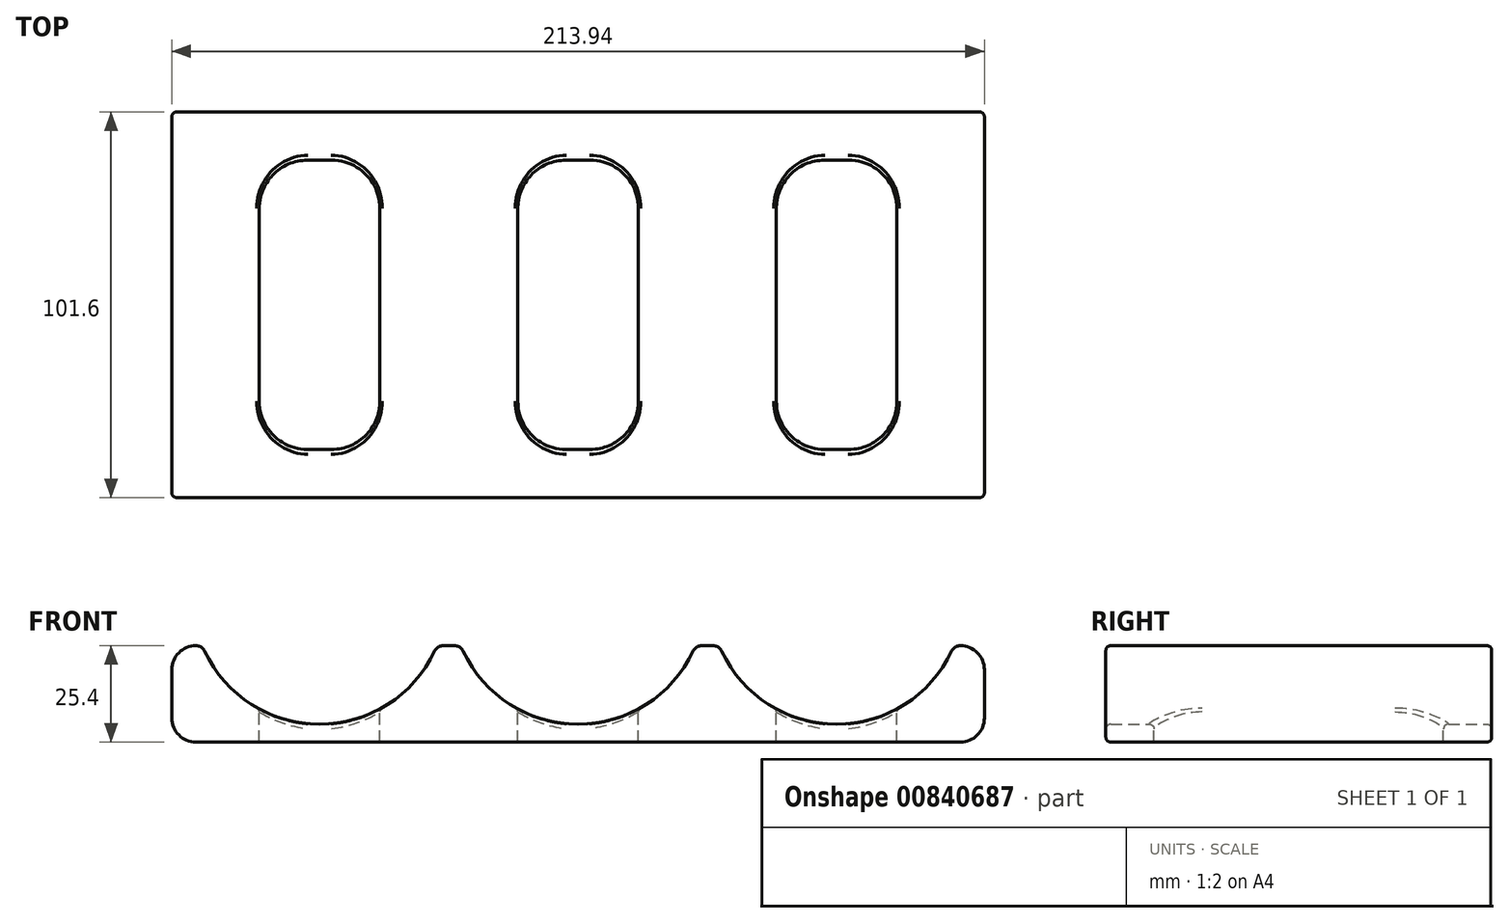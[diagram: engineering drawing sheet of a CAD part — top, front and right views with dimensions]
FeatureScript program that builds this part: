
annotation { "Feature Type Name" : "Feature", "Feature Type Description" : "" }
export const myFeature = defineFeature(function(context is Context, id is Id, definition is map)
    precondition{}
    {
        {
            var Q0;
            Q0=qCreatedBy(makeId("Front.planeOp"),FACE);
            var sketch = newSketch(context, id + "F0", { "sketchPlane" : qUnion([Q0])});
            skCircle(sketch, "E0", {"center": v(0, 0) * mm, "radius": 33.4 * mm, "construction": true});
            skCircle(sketch, "E1", {"center": v(-68.07, 0) * mm, "radius": 33.4 * mm, "construction": true});
            skCircle(sketch, "E2", {"center": v(68.07, 0) * mm, "radius": 33.4 * mm, "construction": true});
            skArc(sketch, "E3", {"start": v(-37.82, -14.16) * mm, "mid": v(-68.07, -33.4) * mm, "end": v(-98.32, -14.16) * mm});
            skArc(sketch, "E4", {"start": v(30.25, -14.16) * mm, "mid": v(0, -33.4) * mm, "end": v(-30.25, -14.16) * mm});
            skArc(sketch, "E5", {"start": v(98.32, -14.16) * mm, "mid": v(68.07, -33.4) * mm, "end": v(37.82, -14.16) * mm});
            skLineSegment(sketch, "E6", {"start": v(-100.62, -12.7) * mm, "end": v(-100.62, -12.7) * mm});
            skLineSegment(sketch, "E7", {"start": v(-100.62, -38.1) * mm, "end": v(100.62, -38.1) * mm});
            skLineSegment(sketch, "E8", {"start": v(-106.97, -19.05) * mm, "end": v(-106.97, -31.75) * mm});
            skLineSegment(sketch, "E9", {"start": v(106.97, -19.05) * mm, "end": v(106.97, -31.75) * mm});
            skPoint(sketch, "E10.orphan", {"position": v(-101.47, 0) * mm});
            skPoint(sketch, "E11.orphan", {"position": v(-34.67, 0) * mm});
            skPoint(sketch, "E12.orphan", {"position": v(-33.4, 0) * mm});
            skPoint(sketch, "E13.orphan", {"position": v(33.4, 0) * mm});
            skPoint(sketch, "E14.orphan", {"position": v(34.67, 0) * mm});
            skPoint(sketch, "E15.orphan", {"position": v(101.47, 0) * mm});
            skLineSegment(sketch, "E16.trimOffspring", {"start": v(-35.52, -12.7) * mm, "end": v(-32.55, -12.7) * mm});
            skLineSegment(sketch, "E17.trimOffspring", {"start": v(32.55, -12.7) * mm, "end": v(35.52, -12.7) * mm});
            skLineSegment(sketch, "E18.trimOffspring", {"start": v(100.62, -12.7) * mm, "end": v(100.62, -12.7) * mm});
            skPoint(sketch, "E19.visualSharp", {"position": v(-98.96, -12.7) * mm});
            skArc(sketch, "E19.filletArc", {"start": v(-98.32, -14.16) * mm, "mid": v(-99.26, -13.1) * mm, "end": v(-100.62, -12.7) * mm});
            skPoint(sketch, "E20.visualSharp", {"position": v(-37.18, -12.7) * mm});
            skArc(sketch, "E20.filletArc", {"start": v(-35.52, -12.7) * mm, "mid": v(-36.89, -13.1) * mm, "end": v(-37.82, -14.16) * mm});
            skPoint(sketch, "E21.visualSharp", {"position": v(-30.9, -12.7) * mm});
            skArc(sketch, "E21.filletArc", {"start": v(-30.25, -14.16) * mm, "mid": v(-31.19, -13.1) * mm, "end": v(-32.55, -12.7) * mm});
            skPoint(sketch, "E22.visualSharp", {"position": v(30.9, -12.7) * mm});
            skArc(sketch, "E22.filletArc", {"start": v(32.55, -12.7) * mm, "mid": v(31.19, -13.1) * mm, "end": v(30.25, -14.16) * mm});
            skPoint(sketch, "E23.visualSharp", {"position": v(37.18, -12.7) * mm});
            skArc(sketch, "E23.filletArc", {"start": v(37.82, -14.16) * mm, "mid": v(36.89, -13.1) * mm, "end": v(35.52, -12.7) * mm});
            skPoint(sketch, "E24.visualSharp", {"position": v(98.96, -12.7) * mm});
            skArc(sketch, "E24.filletArc", {"start": v(100.62, -12.7) * mm, "mid": v(99.26, -13.1) * mm, "end": v(98.32, -14.16) * mm});
            skPoint(sketch, "E25.visualSharp", {"position": v(106.97, -12.7) * mm});
            skArc(sketch, "E25.filletArc", {"start": v(106.97, -19.05) * mm, "mid": v(105.11, -14.56) * mm, "end": v(100.62, -12.7) * mm});
            skPoint(sketch, "E26.visualSharp", {"position": v(106.97, -38.1) * mm});
            skArc(sketch, "E26.filletArc", {"start": v(100.62, -38.1) * mm, "mid": v(105.11, -36.24) * mm, "end": v(106.97, -31.75) * mm});
            skPoint(sketch, "E27.visualSharp", {"position": v(-106.97, -38.1) * mm});
            skArc(sketch, "E27.filletArc", {"start": v(-106.97, -31.75) * mm, "mid": v(-105.11, -36.24) * mm, "end": v(-100.62, -38.1) * mm});
            skPoint(sketch, "E28.visualSharp", {"position": v(-106.97, -12.7) * mm});
            skArc(sketch, "E28.filletArc", {"start": v(-100.62, -12.7) * mm, "mid": v(-105.11, -14.56) * mm, "end": v(-106.97, -19.05) * mm});
            skSolve(sketch);
        }
        {
            var Q0;
            Q0 = qSketchRegion(id + "F0", true);
            extrude(context, id + "F1", {"entities" : qUnion([Q0]), "depth" : 101.6 * mm, "offsetDistance" : 25.4 * mm});
        }
        {
            var Q0;
            Q0=qCreatedBy(makeId("Top.planeOp"),FACE);
            var sketch = newSketch(context, id + "F2", { "sketchPlane" : qUnion([Q0])});
            skLineSegment(sketch, "E29.bottom", {"start": v(-15.88, -12.7) * mm, "end": v(15.88, -12.7) * mm});
            skLineSegment(sketch, "E29.top", {"start": v(-15.87, -88.9) * mm, "end": v(15.87, -88.9) * mm});
            skLineSegment(sketch, "E29.left", {"start": v(-15.88, -12.7) * mm, "end": v(-15.87, -88.9) * mm});
            skLineSegment(sketch, "E29.right", {"start": v(15.88, -12.7) * mm, "end": v(15.87, -88.9) * mm});
            skLineSegment(sketch, "E30.bottom", {"start": v(52.2, -12.7) * mm, "end": v(83.95, -12.7) * mm});
            skLineSegment(sketch, "E30.top", {"start": v(52.2, -88.9) * mm, "end": v(83.95, -88.9) * mm});
            skLineSegment(sketch, "E30.left", {"start": v(52.2, -12.7) * mm, "end": v(52.2, -88.9) * mm});
            skLineSegment(sketch, "E30.right", {"start": v(83.95, -12.7) * mm, "end": v(83.95, -88.9) * mm});
            skLineSegment(sketch, "E31.bottom", {"start": v(-83.95, -12.7) * mm, "end": v(-52.2, -12.7) * mm});
            skLineSegment(sketch, "E31.top", {"start": v(-83.95, -88.9) * mm, "end": v(-52.2, -88.9) * mm});
            skLineSegment(sketch, "E31.left", {"start": v(-83.95, -12.7) * mm, "end": v(-83.95, -88.9) * mm});
            skLineSegment(sketch, "E31.right", {"start": v(-52.2, -12.7) * mm, "end": v(-52.2, -88.9) * mm});
            skPoint(sketch, "E32", {"position": v(68.07, -12.7) * mm});
            skPoint(sketch, "E33", {"position": v(0, -12.7) * mm});
            skPoint(sketch, "E34", {"position": v(-68.07, -12.7) * mm});
            skSolve(sketch);
        }
        {
            var Q0;
            Q0 = qSketchRegion(id + "F2", true);
            extrude(context, id + "F3", {"entities" : qUnion([Q0]), "operationType" : NewBodyOperationType.REMOVE, "endBound" : BoundingType.THROUGH_ALL, "oppositeDirection" : true, "depth" : 25.4 * mm, "offsetDistance" : 25.4 * mm});
        }
        {
            var Q0;
            Q0=makeQuery(id+"F3.boolean.opBoolean","COPY",EDGE,{"derivedFrom":makeQuery(id+"F3.opExtrude","SWEPT_EDGE",EDGE,{"disambiguationData":[OSD([sQuery(id+"F2.wireOp",EDGE,"E31.bottom"),sQuery(id+"F2.wireOp",EDGE,"E31.left")])]})});
            var Q1;
            Q1=makeQuery(id+"F3.boolean.opBoolean","COPY",EDGE,{"derivedFrom":makeQuery(id+"F3.opExtrude","SWEPT_EDGE",EDGE,{"disambiguationData":[OSD([sQuery(id+"F2.wireOp",EDGE,"E31.bottom"),sQuery(id+"F2.wireOp",EDGE,"E31.right")])]})});
            var Q2;
            Q2=makeQuery(id+"F3.boolean.opBoolean","COPY",EDGE,{"derivedFrom":makeQuery(id+"F3.opExtrude","SWEPT_EDGE",EDGE,{"disambiguationData":[OSD([sQuery(id+"F2.wireOp",EDGE,"E31.top"),sQuery(id+"F2.wireOp",EDGE,"E31.left")])]})});
            var Q3;
            Q3=makeQuery(id+"F3.boolean.opBoolean","COPY",EDGE,{"derivedFrom":makeQuery(id+"F3.opExtrude","SWEPT_EDGE",EDGE,{"disambiguationData":[OSD([sQuery(id+"F2.wireOp",EDGE,"E31.top"),sQuery(id+"F2.wireOp",EDGE,"E31.right")])]})});
            var Q4;
            Q4=makeQuery(id+"F3.boolean.opBoolean","COPY",EDGE,{"derivedFrom":makeQuery(id+"F3.opExtrude","SWEPT_EDGE",EDGE,{"disambiguationData":[OSD([sQuery(id+"F2.wireOp",EDGE,"E29.top"),sQuery(id+"F2.wireOp",EDGE,"E29.right")])]})});
            var Q5;
            Q5=makeQuery(id+"F3.boolean.opBoolean","COPY",EDGE,{"derivedFrom":makeQuery(id+"F3.opExtrude","SWEPT_EDGE",EDGE,{"disambiguationData":[OSD([sQuery(id+"F2.wireOp",EDGE,"E29.bottom"),sQuery(id+"F2.wireOp",EDGE,"E29.right")])]})});
            var Q6;
            Q6=makeQuery(id+"F3.boolean.opBoolean","COPY",EDGE,{"derivedFrom":makeQuery(id+"F3.opExtrude","SWEPT_EDGE",EDGE,{"disambiguationData":[OSD([sQuery(id+"F2.wireOp",EDGE,"E29.bottom"),sQuery(id+"F2.wireOp",EDGE,"E29.left")])]})});
            var Q7;
            Q7=makeQuery(id+"F3.boolean.opBoolean","COPY",EDGE,{"derivedFrom":makeQuery(id+"F3.opExtrude","SWEPT_EDGE",EDGE,{"disambiguationData":[OSD([sQuery(id+"F2.wireOp",EDGE,"E29.top"),sQuery(id+"F2.wireOp",EDGE,"E29.left")])]})});
            var Q8;
            Q8=makeQuery(id+"F3.boolean.opBoolean","COPY",EDGE,{"derivedFrom":makeQuery(id+"F3.opExtrude","SWEPT_EDGE",EDGE,{"disambiguationData":[OSD([sQuery(id+"F2.wireOp",EDGE,"E30.bottom"),sQuery(id+"F2.wireOp",EDGE,"E30.left")])]})});
            var Q9;
            Q9=makeQuery(id+"F3.boolean.opBoolean","COPY",EDGE,{"derivedFrom":makeQuery(id+"F3.opExtrude","SWEPT_EDGE",EDGE,{"disambiguationData":[OSD([sQuery(id+"F2.wireOp",EDGE,"E30.bottom"),sQuery(id+"F2.wireOp",EDGE,"E30.right")])]})});
            var Q10;
            Q10=makeQuery(id+"F3.boolean.opBoolean","COPY",EDGE,{"derivedFrom":makeQuery(id+"F3.opExtrude","SWEPT_EDGE",EDGE,{"disambiguationData":[OSD([sQuery(id+"F2.wireOp",EDGE,"E30.top"),sQuery(id+"F2.wireOp",EDGE,"E30.right")])]})});
            var Q11;
            Q11=makeQuery(id+"F3.boolean.opBoolean","COPY",EDGE,{"derivedFrom":makeQuery(id+"F3.opExtrude","SWEPT_EDGE",EDGE,{"disambiguationData":[OSD([sQuery(id+"F2.wireOp",EDGE,"E30.top"),sQuery(id+"F2.wireOp",EDGE,"E30.left")])]})});
            fillet(context, id + "F4", {"entities" : qUnion([Q0, Q1, Q2, Q3, Q4, Q5, Q6, Q7, Q8, Q9, Q10, Q11]), "radius" : 12.7 * mm, "tangentPropagation" : true, "allowEdgeOverflow" : false});
        }
        {
            var Q0;
            Q0=makeQuery(id+"F1.opExtrude","CAP_EDGE",EDGE,{"disambiguationData":[OSD([sQuery(id+"F0.wireOp",EDGE,"E3")])],"isStart":false});
            var Q1;
            Q1=makeQuery(id+"F1.opExtrude","CAP_EDGE",EDGE,{"disambiguationData":[OSD([sQuery(id+"F0.wireOp",EDGE,"E4")])],"isStart":false});
            var Q2;
            Q2=makeQuery(id+"F1.opExtrude","CAP_EDGE",EDGE,{"disambiguationData":[OSD([sQuery(id+"F0.wireOp",EDGE,"E16.trimOffspring")])],"isStart":false});
            var Q3;
            Q3=makeQuery(id+"F1.opExtrude","CAP_EDGE",EDGE,{"disambiguationData":[OSD([sQuery(id+"F0.wireOp",EDGE,"E9")])],"isStart":true});
            var Q4;
            Q4=makeQuery(id+"F1.opExtrude","CAP_EDGE",EDGE,{"disambiguationData":[OSD([sQuery(id+"F0.wireOp",EDGE,"E5")])],"isStart":true});
            var Q5;
            Q5=makeQuery(id+"F3.boolean.opBoolean","INTERSECT",EDGE,{"derivedFrom":[makeQuery(id+"F1.opExtrude","SWEPT_FACE",FACE,{"disambiguationData":[OSD([sQuery(id+"F0.wireOp",EDGE,"E3")])]}),makeQuery(id+"F3.opExtrude","SWEPT_FACE",FACE,{"disambiguationData":[OSD([sQuery(id+"F2.wireOp",EDGE,"E31.right")])]})]});
            var Q6;
            Q6=makeQuery(id+"F4.opFillet","BLEND_EDGE",EDGE,{"blendedFrom":[makeQuery(id+"F3.boolean.opBoolean","COPY",EDGE,{"derivedFrom":makeQuery(id+"F3.opExtrude","SWEPT_EDGE",EDGE,{"disambiguationData":[OSD([sQuery(id+"F2.wireOp",EDGE,"E31.top"),sQuery(id+"F2.wireOp",EDGE,"E31.right")])]})}),makeQuery(id+"F1.opExtrude","SWEPT_FACE",FACE,{"disambiguationData":[OSD([sQuery(id+"F0.wireOp",EDGE,"E3")])]})],"blendedInto":[makeQuery(id+"F1.opExtrude","SWEPT_FACE",FACE,{"disambiguationData":[OSD([sQuery(id+"F0.wireOp",EDGE,"E3")])]})]});
            var Q7;
            Q7=makeQuery(id+"F3.boolean.opBoolean","INTERSECT",EDGE,{"derivedFrom":[makeQuery(id+"F1.opExtrude","SWEPT_FACE",FACE,{"disambiguationData":[OSD([sQuery(id+"F0.wireOp",EDGE,"E4")])]}),makeQuery(id+"F3.opExtrude","SWEPT_FACE",FACE,{"disambiguationData":[OSD([sQuery(id+"F2.wireOp",EDGE,"E29.right")])]})]});
            var Q8;
            Q8=makeQuery(id+"F4.opFillet","BLEND_EDGE",EDGE,{"blendedFrom":[makeQuery(id+"F3.boolean.opBoolean","COPY",EDGE,{"derivedFrom":makeQuery(id+"F3.opExtrude","SWEPT_EDGE",EDGE,{"disambiguationData":[OSD([sQuery(id+"F2.wireOp",EDGE,"E30.top"),sQuery(id+"F2.wireOp",EDGE,"E30.right")])]})}),makeQuery(id+"F1.opExtrude","SWEPT_FACE",FACE,{"disambiguationData":[OSD([sQuery(id+"F0.wireOp",EDGE,"E5")])]})],"blendedInto":[makeQuery(id+"F1.opExtrude","SWEPT_FACE",FACE,{"disambiguationData":[OSD([sQuery(id+"F0.wireOp",EDGE,"E5")])]})]});
            var Q9;
            Q9=makeQuery(id+"F3.boolean.opBoolean","INTERSECT",EDGE,{"derivedFrom":[makeQuery(id+"F1.opExtrude","SWEPT_FACE",FACE,{"disambiguationData":[OSD([sQuery(id+"F0.wireOp",EDGE,"E5")])]}),makeQuery(id+"F3.opExtrude","SWEPT_FACE",FACE,{"disambiguationData":[OSD([sQuery(id+"F2.wireOp",EDGE,"E30.right")])]})]});
            fillet(context, id + "F5", {"entities" : qUnion([Q0, Q1, Q2, Q3, Q4, Q5, Q6, Q7, Q8, Q9]), "radius" : 1.27 * mm, "tangentPropagation" : true, "allowEdgeOverflow" : false});
        }
    });
